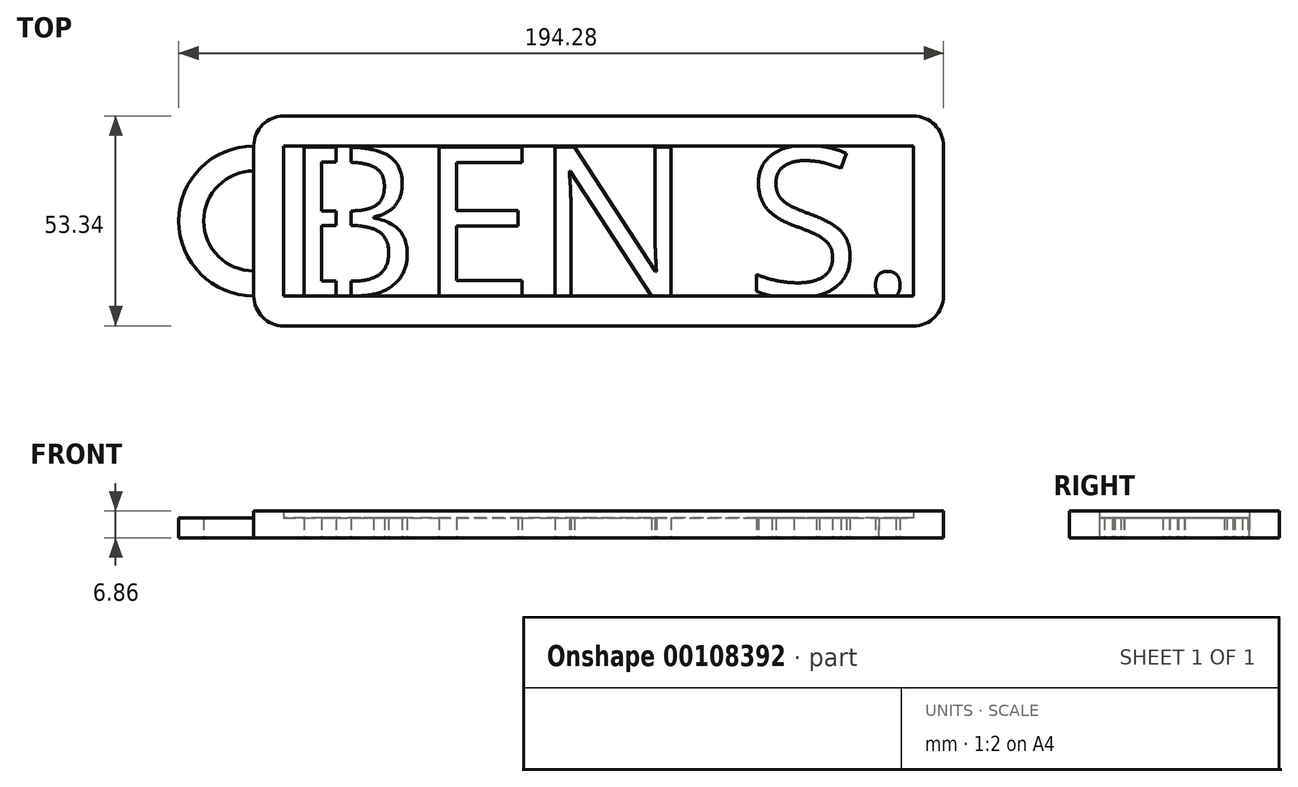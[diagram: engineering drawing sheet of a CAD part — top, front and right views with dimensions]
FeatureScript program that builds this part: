
annotation { "Feature Type Name" : "Feature", "Feature Type Description" : "" }
export const myFeature = defineFeature(function(context is Context, id is Id, definition is map)
    precondition{}
    {
        {
            var Q0;
            Q0=qCreatedBy(makeId("Top.planeOp"),FACE);
            var sketch = newSketch(context, id + "F0", { "sketchPlane" : qUnion([Q0])});
            skLineSegment(sketch, "E0", {"start": v(0, 0) * mm, "end": v(-94.66, 0) * mm});
            skLineSegment(sketch, "E1", {"start": v(0, 0) * mm, "end": v(65.33, 0) * mm});
            skLineSegment(sketch, "E2", {"start": v(-94.66, 0) * mm, "end": v(-94.66, 38.1) * mm});
            skLineSegment(sketch, "E3", {"start": v(65.33, 0) * mm, "end": v(65.33, 38.1) * mm});
            skLineSegment(sketch, "E4", {"start": v(65.33, 38.1) * mm, "end": v(-94.66, 38.1) * mm});
            skLineSegment(sketch, "E5", {"start": v(-94.66, 38.1) * mm, "end": v(-94.66, 45.72) * mm});
            skLineSegment(sketch, "E6", {"start": v(-94.66, 45.72) * mm, "end": v(-94.66, 38.1) * mm});
            skLineSegment(sketch, "E7", {"start": v(-94.66, 38.1) * mm, "end": v(-102.28, 38.1) * mm});
            skLineSegment(sketch, "E8", {"start": v(-94.66, 0) * mm, "end": v(-102.28, 0) * mm});
            skLineSegment(sketch, "E9", {"start": v(-102.28, 0) * mm, "end": v(-94.66, 0) * mm});
            skLineSegment(sketch, "E10", {"start": v(-94.66, 0) * mm, "end": v(-94.66, -7.62) * mm});
            skLineSegment(sketch, "E11", {"start": v(65.33, 0) * mm, "end": v(65.33, -7.62) * mm});
            skLineSegment(sketch, "E12", {"start": v(65.33, 0) * mm, "end": v(72.95, 0) * mm});
            skLineSegment(sketch, "E13", {"start": v(65.33, 38.1) * mm, "end": v(72.95, 38.1) * mm});
            skLineSegment(sketch, "E14", {"start": v(65.33, 38.1) * mm, "end": v(65.33, 45.72) * mm});
            skLineSegment(sketch, "E15", {"start": v(65.33, 45.72) * mm, "end": v(-94.66, 45.72) * mm});
            skLineSegment(sketch, "E16", {"start": v(-102.28, 0) * mm, "end": v(-102.28, 38.1) * mm});
            skLineSegment(sketch, "E17", {"start": v(-94.66, -7.62) * mm, "end": v(65.33, -7.62) * mm});
            skLineSegment(sketch, "E18", {"start": v(72.95, 0) * mm, "end": v(72.95, 38.1) * mm});
            skArc(sketch, "E19", {"start": v(65.33, -7.62) * mm, "mid": v(70.72, -5.39) * mm, "end": v(72.95, 0) * mm});
            skArc(sketch, "E20", {"start": v(72.95, 38.1) * mm, "mid": v(70.72, 43.49) * mm, "end": v(65.33, 45.72) * mm});
            skArc(sketch, "E21", {"start": v(-94.66, 45.72) * mm, "mid": v(-100.05, 43.49) * mm, "end": v(-102.28, 38.1) * mm});
            skArc(sketch, "E22", {"start": v(-102.28, 0) * mm, "mid": v(-100.05, -5.39) * mm, "end": v(-94.66, -7.62) * mm});
            skArc(sketch, "E23", {"start": v(-94.66, 36.5) * mm, "mid": v(-121.33, 19.05) * mm, "end": v(-94.66, 1.6) * mm});
            skArc(sketch, "E24", {"start": v(-94.66, 29.2) * mm, "mid": v(-114.98, 19.05) * mm, "end": v(-94.66, 8.9) * mm});
            skLineSegment(sketch, "E25", {"start": v(-81.38, 38.1) * mm, "end": v(-81.38, 0) * mm});
            skLineSegment(sketch, "E26", {"start": v(-77.57, 38.1) * mm, "end": v(-77.57, 0) * mm});
            skText(sketch, "E27", { "text": "BEN S.", "fontName": "OpenSans-Regular.ttf"});
            const initialGuessF0  = {"E27": [-0.09466, 0, 1, 0, 0.0381]};
            skSetInitialGuess(sketch, initialGuessF0);
            skSolve(sketch);
        }
        {
            var Q0;
            Q0=qCreatedBy(makeId("Top.planeOp"),FACE);
            var sketch = newSketch(context, id + "F1", { "sketchPlane" : qUnion([Q0])});
            skLineSegment(sketch, "E28", {"start": v(0, 0) * mm, "end": v(-94.67, 0) * mm});
            skLineSegment(sketch, "E29", {"start": v(0, 0) * mm, "end": v(65.33, 0) * mm});
            skLineSegment(sketch, "E30", {"start": v(-94.67, 0) * mm, "end": v(-94.67, 38.1) * mm});
            skLineSegment(sketch, "E31", {"start": v(65.33, 0) * mm, "end": v(65.33, 38.1) * mm});
            skLineSegment(sketch, "E32", {"start": v(65.33, 38.1) * mm, "end": v(-94.67, 38.1) * mm});
            skLineSegment(sketch, "E33", {"start": v(-94.67, 38.1) * mm, "end": v(-94.67, 45.72) * mm});
            skLineSegment(sketch, "E34", {"start": v(-94.67, 0) * mm, "end": v(-94.67, -7.62) * mm});
            skLineSegment(sketch, "E35", {"start": v(-94.67, 0) * mm, "end": v(-102.29, 0) * mm});
            skLineSegment(sketch, "E36", {"start": v(65.33, 0) * mm, "end": v(65.33, -7.62) * mm});
            skLineSegment(sketch, "E37", {"start": v(65.33, 0) * mm, "end": v(72.95, 0) * mm});
            skLineSegment(sketch, "E38", {"start": v(65.33, 38.1) * mm, "end": v(65.33, 45.72) * mm});
            skLineSegment(sketch, "E39", {"start": v(65.33, 38.1) * mm, "end": v(72.95, 38.1) * mm});
            skLineSegment(sketch, "E40", {"start": v(-94.67, 38.1) * mm, "end": v(-102.29, 38.1) * mm});
            skLineSegment(sketch, "E41", {"start": v(65.33, 45.72) * mm, "end": v(-94.67, 45.72) * mm});
            skLineSegment(sketch, "E42", {"start": v(-102.29, 38.1) * mm, "end": v(-102.29, 0) * mm});
            skLineSegment(sketch, "E43", {"start": v(-94.67, -7.62) * mm, "end": v(65.33, -7.62) * mm});
            skLineSegment(sketch, "E44", {"start": v(72.95, 0) * mm, "end": v(72.95, 38.1) * mm});
            skArc(sketch, "E45", {"start": v(72.95, 38.1) * mm, "mid": v(70.72, 43.49) * mm, "end": v(65.33, 45.72) * mm});
            skArc(sketch, "E46", {"start": v(-94.67, 45.72) * mm, "mid": v(-100.05, 43.49) * mm, "end": v(-102.29, 38.1) * mm});
            skArc(sketch, "E47", {"start": v(-102.29, 0) * mm, "mid": v(-100.05, -5.39) * mm, "end": v(-94.67, -7.62) * mm});
            skArc(sketch, "E48", {"start": v(65.33, -7.62) * mm, "mid": v(70.72, -5.39) * mm, "end": v(72.95, 0) * mm});
            skSolve(sketch);
        }
        {
            var Q0;
            Q0 = qSketchRegion(id + "F1", true);
            extrude(context, id + "F2", {"entities" : qUnion([Q0]), "depth" : 6.86 * mm});
        }
        {
            var Q0;
            Q0 = qSketchRegion(id + "F0", true);
            var Q1;
            {var subQ1=sQuery(id+"F0.wireOp",EDGE,"E4");var subQ7=sQuery(id+"F0.wireOp",EDGE,"E25");var subQ9=makeQuery(id+"F0.imprint","INTERSECT",VERTEX,{"derivedFrom":[subQ1,subQ7]});Q1=makeQuery(id+"F0.imprint","IMPRINT",FACE,{"disambiguationData":[TD([[makeQuery(id+"F0.imprint","IMPRINT",EDGE,{"disambiguationData":[TD([[subQ9,1.0]])],"derivedFrom":subQ1}),1.0]])]});}
            var Q2;
            {var subQ5=sQuery(id+"F0.wireOp",EDGE,"E27.sketch_text.stroke-0");var subQ7=sQuery(id+"F0.wireOp",EDGE,"E25");var subQ8=makeQuery(id+"F0.imprint","INTERSECT",VERTEX,{"derivedFrom":[subQ7,subQ5]});Q2=makeQuery(id+"F0.imprint","IMPRINT",FACE,{"disambiguationData":[TD([[makeQuery(id+"F0.imprint","IMPRINT",EDGE,{"disambiguationData":[TD([[subQ8,-1.0]])],"derivedFrom":subQ7}),1.0]])]});}
            var Q3;
            {var subQ1=sQuery(id+"F0.wireOp",EDGE,"E27.sketch_text.stroke-11");var subQ6=sQuery(id+"F0.wireOp",EDGE,"E25");var subQ9=makeQuery(id+"F0.imprint","INTERSECT",VERTEX,{"derivedFrom":[subQ6,subQ1]});Q3=makeQuery(id+"F0.imprint","IMPRINT",FACE,{"disambiguationData":[TD([[makeQuery(id+"F0.imprint","IMPRINT",EDGE,{"disambiguationData":[TD([[subQ9,-1.0]])],"derivedFrom":subQ6}),1.0]])]});}
            var Q4;
            {var subQ0=sQuery(id+"F0.wireOp",EDGE,"E27.sketch_text.stroke-9");var subQ1=sQuery(id+"F0.wireOp",EDGE,"E25");var subQ2=makeQuery(id+"F0.imprint","INTERSECT",VERTEX,{"derivedFrom":[subQ1,subQ0]});Q4=makeQuery(id+"F0.imprint","IMPRINT",FACE,{"disambiguationData":[TD([[makeQuery(id+"F0.imprint","IMPRINT",EDGE,{"disambiguationData":[TD([[subQ2,1.0]])],"derivedFrom":subQ1}),1.0]])]});}
            var Q5;
            {var subQ5=sQuery(id+"F0.wireOp",EDGE,"E25");var subQ9=sQuery(id+"F0.wireOp",EDGE,"E27.sketch_text.stroke-16");var subQ10=makeQuery(id+"F0.imprint","INTERSECT",VERTEX,{"derivedFrom":[subQ5,subQ9]});Q5=makeQuery(id+"F0.imprint","IMPRINT",FACE,{"disambiguationData":[TD([[makeQuery(id+"F0.imprint","IMPRINT",EDGE,{"disambiguationData":[TD([[subQ10,-1.0]])],"derivedFrom":subQ5}),1.0]])]});}
            var Q6;
            {var subQ0=sQuery(id+"F0.wireOp",EDGE,"E27.sketch_text.stroke-24");var subQ1=sQuery(id+"F0.wireOp",EDGE,"E25");var subQ2=makeQuery(id+"F0.imprint","INTERSECT",VERTEX,{"derivedFrom":[subQ1,subQ0]});Q6=makeQuery(id+"F0.imprint","IMPRINT",FACE,{"disambiguationData":[TD([[makeQuery(id+"F0.imprint","IMPRINT",EDGE,{"disambiguationData":[TD([[subQ2,-1.0]])],"derivedFrom":subQ1}),1.0]])]});}
            var Q7;
            {var subQ5=sQuery(id+"F0.wireOp",EDGE,"E27.sketch_text.stroke-18");Q7=makeQuery(id+"F0.imprint","IMPRINT",FACE,{"disambiguationData":[TD([[makeQuery(id+"F0.imprint","IMPRINT",EDGE,{"derivedFrom":subQ5}),1.0]])]});}
            var Q8;
            {var subQ0=sQuery(id+"F0.wireOp",EDGE,"E27.sketch_text.stroke-20");Q8=makeQuery(id+"F0.imprint","IMPRINT",FACE,{"disambiguationData":[TD([[makeQuery(id+"F0.imprint","IMPRINT",EDGE,{"derivedFrom":subQ0}),1.0]])]});}
            var Q9;
            {var subQ1=sQuery(id+"F0.wireOp",EDGE,"E27.sketch_text.stroke-13");Q9=makeQuery(id+"F0.imprint","IMPRINT",FACE,{"disambiguationData":[TD([[makeQuery(id+"F0.imprint","IMPRINT",EDGE,{"derivedFrom":subQ1}),1.0]])]});}
            var Q10;
            {var subQ5=sQuery(id+"F0.wireOp",EDGE,"E27.sketch_text.stroke-17");Q10=makeQuery(id+"F0.imprint","IMPRINT",FACE,{"disambiguationData":[TD([[makeQuery(id+"F0.imprint","IMPRINT",EDGE,{"derivedFrom":subQ5}),1.0]])]});}
            var Q11;
            {var subQ8=sQuery(id+"F0.wireOp",EDGE,"E27.sketch_text.stroke-10");Q11=makeQuery(id+"F0.imprint","IMPRINT",FACE,{"disambiguationData":[TD([[makeQuery(id+"F0.imprint","IMPRINT",EDGE,{"derivedFrom":subQ8}),1.0]])]});}
            var Q12;
            {var subQ17=sQuery(id+"F0.wireOp",EDGE,"E27.sketch_text.stroke-2");Q12=makeQuery(id+"F0.imprint","IMPRINT",FACE,{"disambiguationData":[TD([[makeQuery(id+"F0.imprint","IMPRINT",EDGE,{"derivedFrom":subQ17}),1.0]])]});}
            var Q13;
            {var subQ9=sQuery(id+"F0.wireOp",EDGE,"E3");Q13=makeQuery(id+"F0.imprint","IMPRINT",FACE,{"disambiguationData":[TD([[makeQuery(id+"F0.imprint","IMPRINT",EDGE,{"derivedFrom":subQ9}),1.0]])]});}
            var Q14;
            {var subQ0=sQuery(id+"F0.wireOp",EDGE,"E27.sketch_text.stroke-38");Q14=makeQuery(id+"F0.imprint","IMPRINT",FACE,{"disambiguationData":[TD([[makeQuery(id+"F0.imprint","IMPRINT",EDGE,{"derivedFrom":subQ0}),1.0]])]});}
            extrude(context, id + "F3", {"entities" : qUnion([Q0, Q1, Q2, Q3, Q4, Q5, Q6, Q7, Q8, Q9, Q10, Q11, Q12, Q13, Q14]), "operationType" : NewBodyOperationType.ADD, "depth" : 5.08 * mm});
        }
    });
